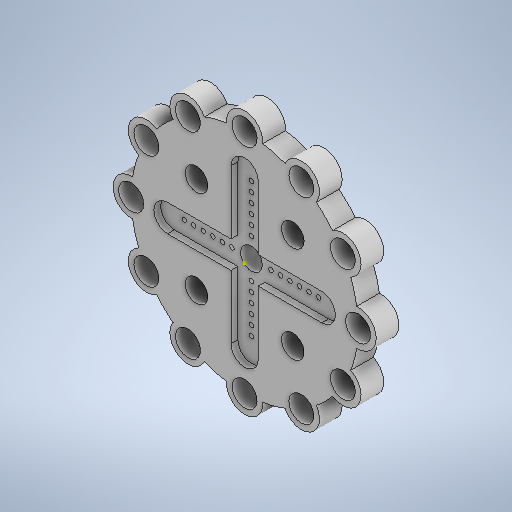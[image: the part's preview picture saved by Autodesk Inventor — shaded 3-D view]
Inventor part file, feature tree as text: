
AUTODESK INVENTOR PART (.ipt)
format: ipt  version: 2025.2 (Build 292293000, 293)  size: 425,984 bytes
history: native  units: mm
features: sketch x12, extrude x8, pattern_circular x3, other x2, hole x1
ambient origin geometry x8: Origin, YZ Plane, XZ Plane, XY Plane, X Axis, Y Axis, Z Axis, Center Point
bodies: Body1 (feature_tree)
feature tree (26):
  other  "Bryła1"
  extrude  "Wyciągnięcie proste1"  Depth=50.0mm
  sketch  "Szkic3"
  extrude  "Wyciągnięcie proste2"  Depth=5.0mm TaperAngle=0.0deg
  sketch  "Szkic7"
  extrude  "Wyciągnięcie proste3"  Depth=4.8mm
  extrude  "Wyciągnięcie proste4"  Depth=5.0mm TaperAngle=0.0deg
  pattern_circular  "Szyk kołowy1"  [2 undecoded]
  hole  "Otwór2"  [1 undecoded]
  pattern_circular  "Szyk kołowy2"  [2 undecoded]
  extrude  "Wyciągnięcie proste8"  Depth=120.0mm TaperAngle=360.0deg
  extrude  "Wyciągnięcie proste9"  Depth=5.0mm TaperAngle=0.0deg
  extrude  "Wyciągnięcie proste10"  Depth=5.5mm
  pattern_circular  "Szyk kołowy3"  [2 undecoded]
  extrude  "Wyciągnięcie proste11"  Depth=120.0mm TaperAngle=360.0deg
  sketch  "Szkic27"
  sketch  "Szkic1"
  sketch  "Szkic4"
  sketch  "Szkic11"
  other  "Kołowy szyk szkicu1"
  sketch  "Szkic16"
  sketch  "Szkic22"
  sketch  "Szkic23"
  sketch  "Szkic24"
  sketch  "Szkic25"
  sketch  "Szkic26"
note: 7 required parameter values undecoded (feature->parameter linkage not recoverable at this tier; creation-order binding heuristic only, values carry confidence <= 0.55)
